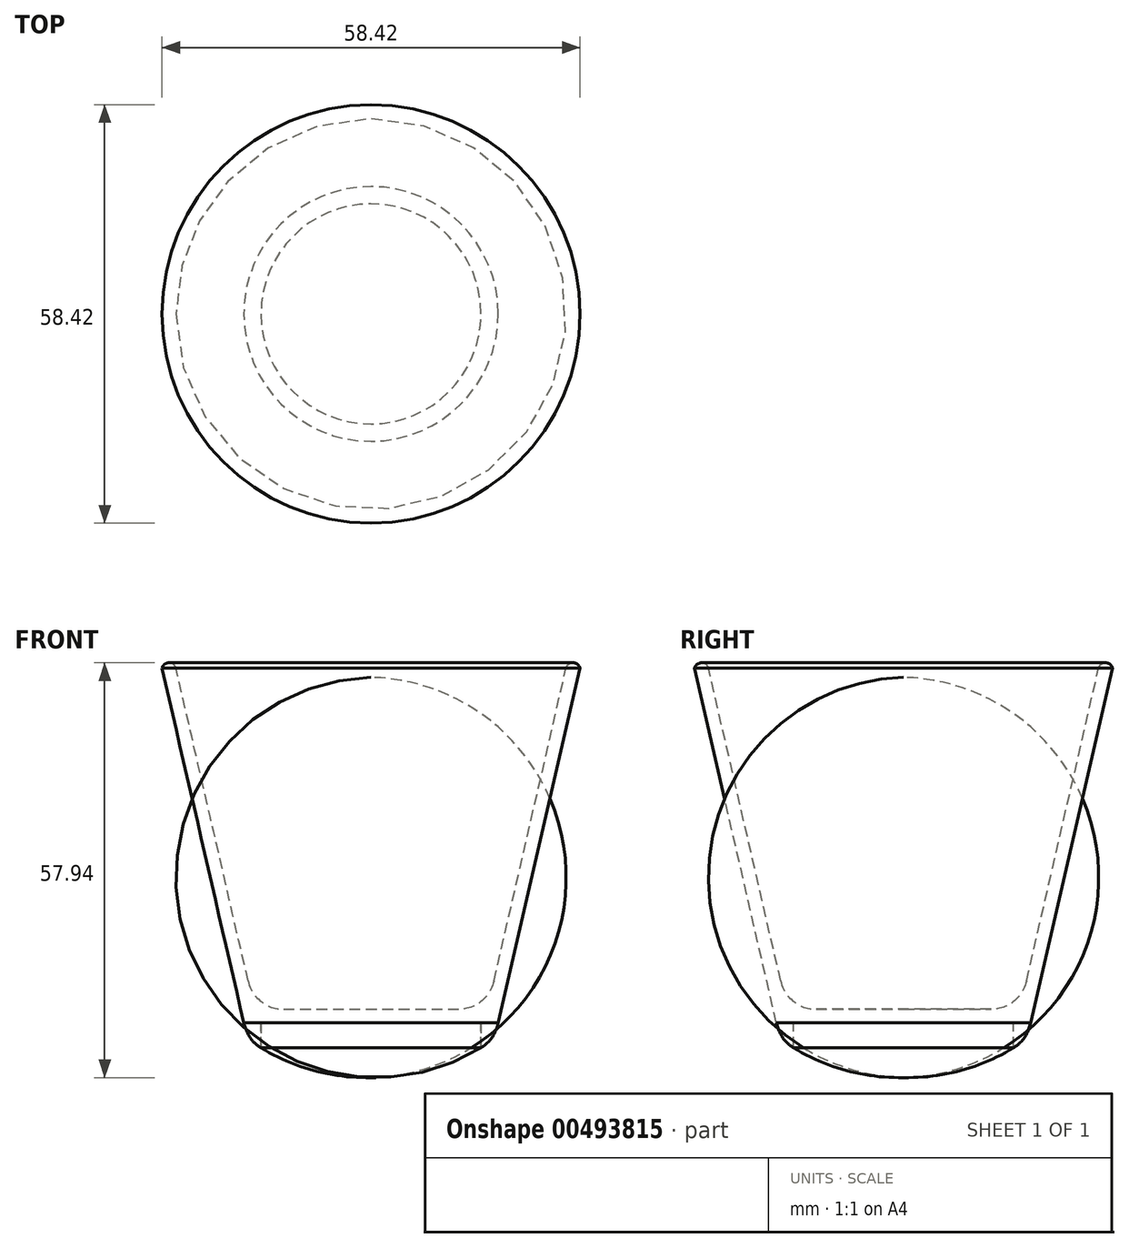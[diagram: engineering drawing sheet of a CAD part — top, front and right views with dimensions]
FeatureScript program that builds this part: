
annotation { "Feature Type Name" : "Feature", "Feature Type Description" : "" }
export const myFeature = defineFeature(function(context is Context, id is Id, definition is map)
    precondition{}
    {
        {
            var Q0;
            Q0=qCreatedBy(makeId("Front.planeOp"),FACE);
            var sketch = newSketch(context, id + "F0", { "sketchPlane" : qUnion([Q0])});
            skLineSegment(sketch, "E0", {"start": v(0, 7.7) * mm, "end": v(0, 57.15) * mm, "construction": true});
            skLineSegment(sketch, "E1", {"start": v(0, 57.15) * mm, "end": v(-29.21, 57.15) * mm, "construction": true});
            skLineSegment(sketch, "E2", {"start": v(-29.21, 57.15) * mm, "end": v(-17.78, 7.65) * mm});
            skFitSpline(sketch, "E3", {"points": [v(-17.78, 7.65) * mm, v(-15.37, 4.16) * mm], "startDerivative": vector(1.75, -6.6) * mm, "endDerivative": vector(2.42, -1.42) * mm});
            skLineSegment(sketch, "E4.0", {"start": v(-27.25, 57.15) * mm, "end": v(-17.17, 13.46) * mm});
            skArc(sketch, "E5", {"start": v(-27.25, 57.15) * mm, "mid": v(-28.23, 57.93) * mm, "end": v(-29.21, 57.15) * mm});
            skLineSegment(sketch, "E6", {"start": v(0, 0) * mm, "end": v(0, 9.53) * mm});
            skLineSegment(sketch, "E7", {"start": v(0, 9.53) * mm, "end": v(-12.22, 9.52) * mm});
            skPoint(sketch, "E8.visualSharp", {"position": v(-16.26, 9.52) * mm});
            skArc(sketch, "E8.filletArc", {"start": v(-17.17, 13.46) * mm, "mid": v(-15.38, 10.63) * mm, "end": v(-12.22, 9.52) * mm});
            skLineSegment(sketch, "E9", {"start": v(-15.37, 4.16) * mm, "end": v(-15.37, 7.7) * mm});
            skLineSegment(sketch, "E10", {"start": v(-15.37, 7.7) * mm, "end": v(0, 7.7) * mm});
            skArc(sketch, "E11", {"start": v(-15.37, 4.16) * mm, "mid": v(-7.99, 0.96) * mm, "end": v(0, 0) * mm});
            skSolve(sketch);
        }
        {
            var Q0;
            Q0=makeQuery(id+"F0.imprint","IMPRINT",FACE,{"disambiguationData":[TD([[makeQuery(id+"F0.imprint","IMPRINT",EDGE,{"derivedFrom":sQuery(id+"F0.wireOp",EDGE,"E2")}),1.0]])]});
            var Q1;
            Q1=sQuery(id+"F0.wireOp",EDGE,"E6");
            revolve(context, id + "F1", {"entities" : qUnion([Q0]), "axis" : qUnion([Q1]), "revolveType" : RevolveType.FULL});
        }
        {
            var Q0;
            Q0=qCreatedBy(makeId("Front.planeOp"),FACE);
            var sketch = newSketch(context, id + "F2", { "sketchPlane" : qUnion([Q0])});
            skArc(sketch, "E12", {"start": v(0, 0) * mm, "mid": v(-7.1, 1.07) * mm, "end": v(-13.56, 4.18) * mm});
            skLineSegment(sketch, "E13", {"start": v(0, 24.1) * mm, "end": v(0, 0) * mm, "construction": true});
            skSolve(sketch);
        }
        {
            var Q0;
            Q0=makeQuery(id+"F0.imprint","IMPRINT",FACE,{"disambiguationData":[TD([[makeQuery(id+"F0.imprint","IMPRINT",EDGE,{"derivedFrom":sQuery(id+"F0.wireOp",EDGE,"E9")}),-1.0]])]});
            var Q1;
            Q1=sQuery(id+"F2.wireOp",EDGE,"E13");
            revolve(context, id + "F3", {"entities" : qUnion([Q0]), "axis" : qUnion([Q1]), "revolveType" : RevolveType.FULL});
        }
    });
